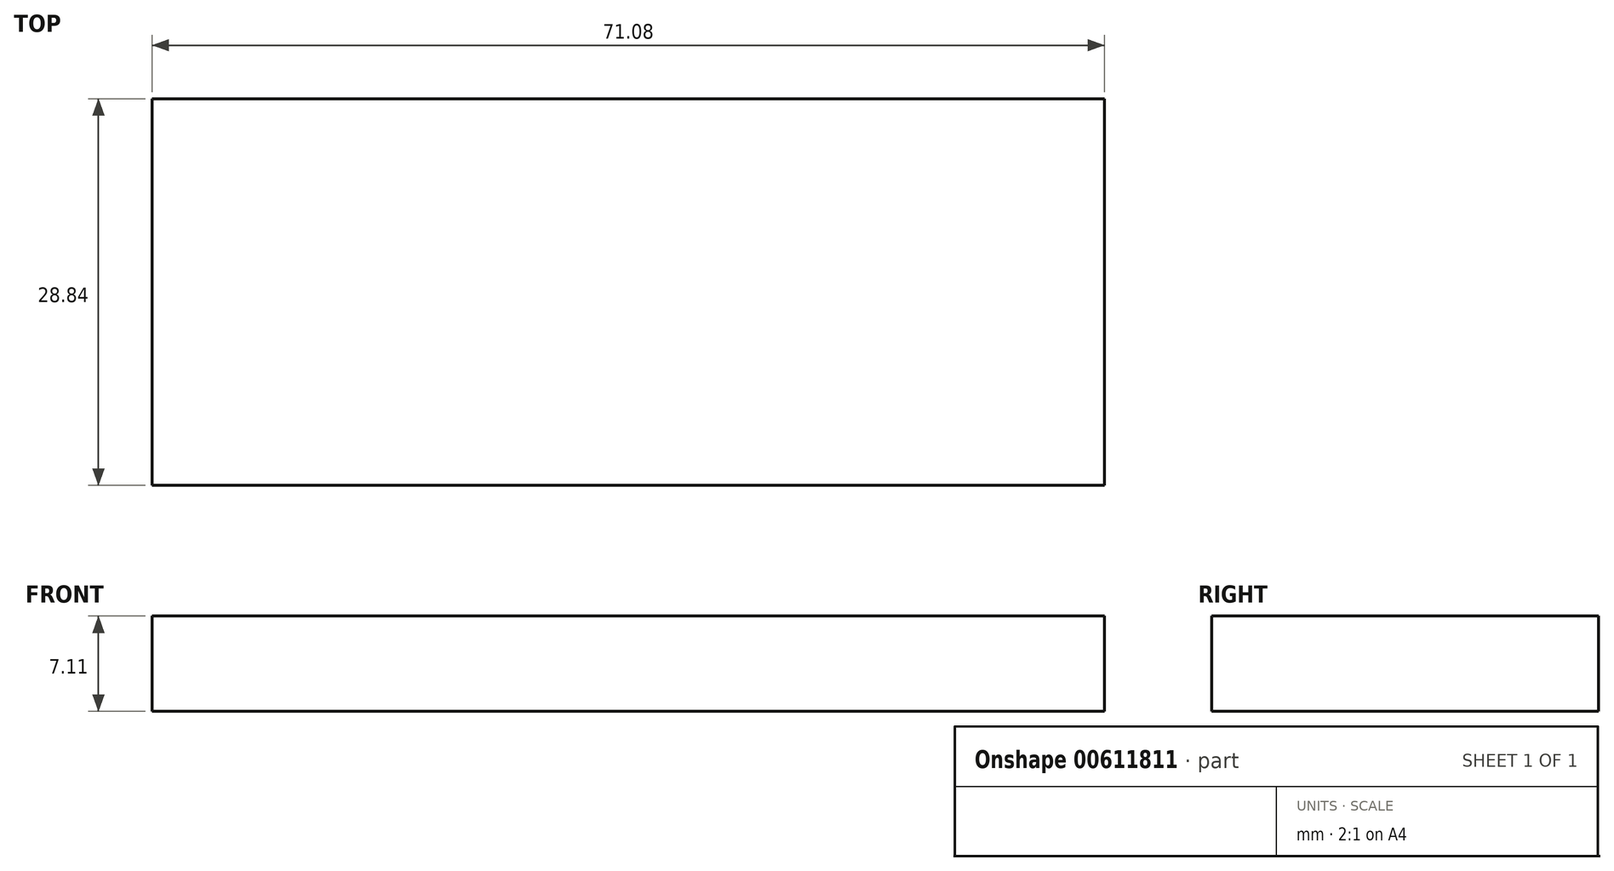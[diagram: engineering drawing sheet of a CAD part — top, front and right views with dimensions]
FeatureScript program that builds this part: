
annotation { "Feature Type Name" : "Feature", "Feature Type Description" : "" }
export const myFeature = defineFeature(function(context is Context, id is Id, definition is map)
    precondition{}
    {
        {
            var Q0;
            Q0=qCreatedBy(makeId("Top.planeOp"),FACE);
            var sketch = newSketch(context, id + "F0", { "sketchPlane" : qUnion([Q0])});
            skLineSegment(sketch, "E0.bottom", {"start": v(35.54, -14.42) * mm, "end": v(-35.54, -14.42) * mm});
            skLineSegment(sketch, "E0.top", {"start": v(35.54, 14.42) * mm, "end": v(-35.54, 14.42) * mm});
            skLineSegment(sketch, "E0.left", {"start": v(35.54, -14.42) * mm, "end": v(35.54, 14.42) * mm});
            skLineSegment(sketch, "E0.right", {"start": v(-35.54, -14.42) * mm, "end": v(-35.54, 14.42) * mm});
            skPoint(sketch, "E0.middle", {"position": v(0, 0) * mm});
            skSolve(sketch);
        }
        {
            var Q0;
            Q0 = qSketchRegion(id + "F0", true);
            extrude(context, id + "F1", {"entities" : qUnion([Q0]), "depth" : 7.11 * mm, "offsetDistance" : 25.4 * mm});
        }
    });
